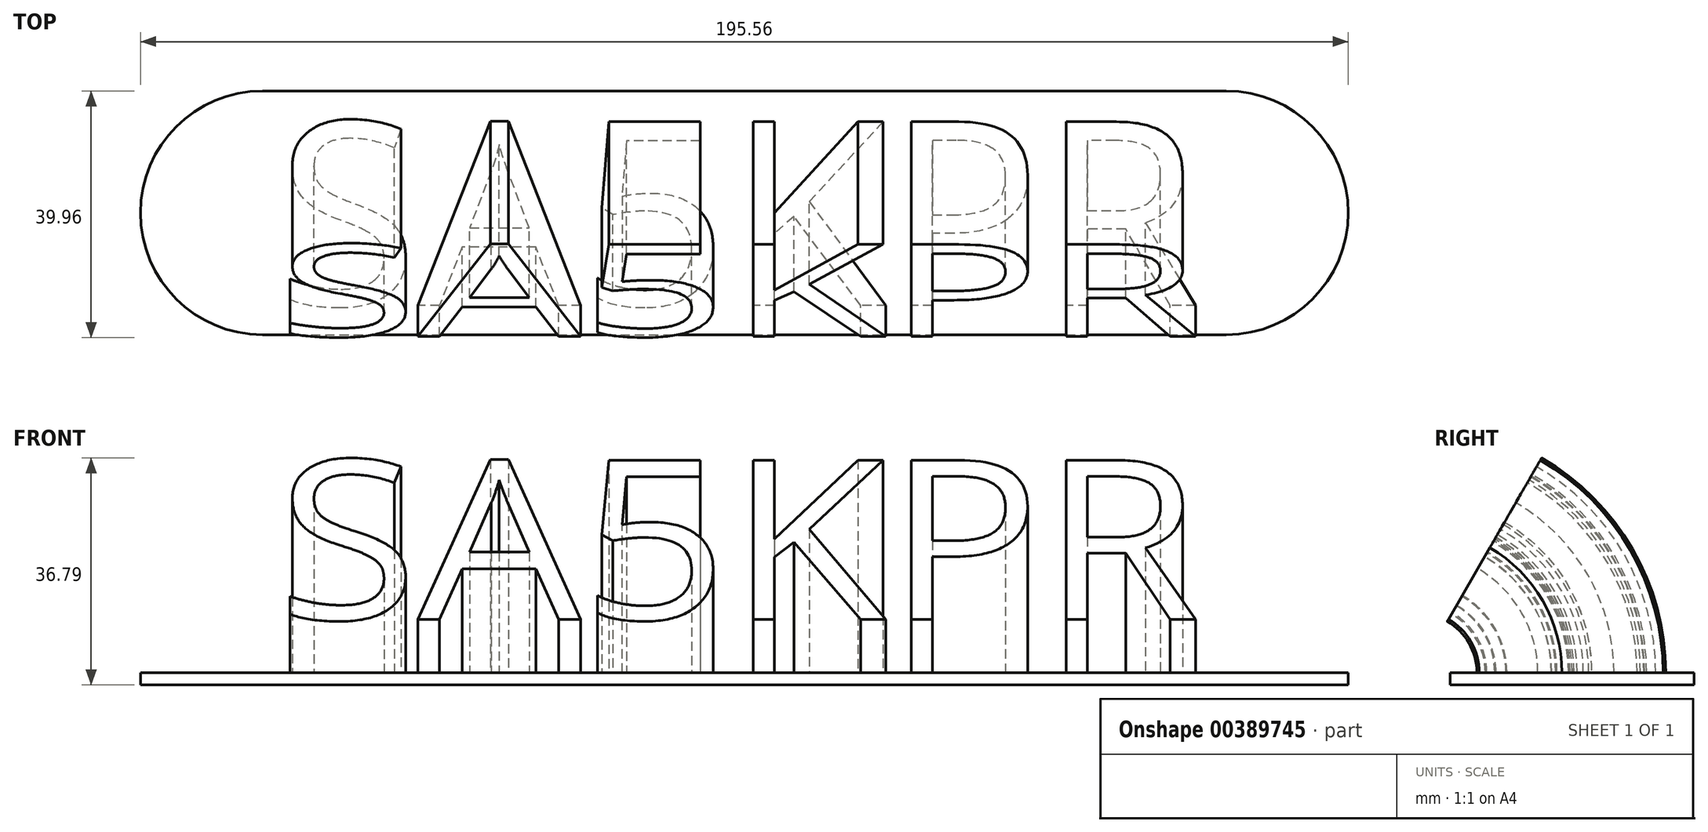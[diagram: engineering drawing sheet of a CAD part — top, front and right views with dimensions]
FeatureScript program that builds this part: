
annotation { "Feature Type Name" : "Feature", "Feature Type Description" : "" }
export const myFeature = defineFeature(function(context is Context, id is Id, definition is map)
    precondition{}
    {
        {
            var Q0;
            Q0=qCreatedBy(makeId("Top.planeOp"),FACE);
            var sketch = newSketch(context, id + "F0", { "sketchPlane" : qUnion([Q0])});
            skText(sketch, "E0", { "text": "SA5KPR", "fontName": "OpenSans-Regular.ttf"});
            skLineSegment(sketch, "E1", {"start": v(-75.73, -25) * mm, "end": v(75.73, -25) * mm});
            const initialGuessF0  = {"E0": [-0.07573, -0.015, 1, 0, 0.03]};
            skSetInitialGuess(sketch, initialGuessF0);
            skSolve(sketch);
        }
        {
            var Q0;
            Q0 = qSketchRegion(id + "F0", true);
            var Q1;
            Q1=sQuery(id+"F0.wireOp",EDGE,"E1");
            revolve(context, id + "F1", {"entities" : qUnion([Q0]), "axis" : qUnion([Q1]), "revolveType" : RevolveType.ONE_DIRECTION, "angle" : 60 * degree});
        }
        {
            var Q0;
            Q0=qCreatedBy(makeId("Top.planeOp"),FACE);
            var sketch = newSketch(context, id + "F2", { "sketchPlane" : qUnion([Q0])});
            skLineSegment(sketch, "E2", {"start": v(-78.03, -19.75) * mm, "end": v(78.03, -19.75) * mm});
            skLineSegment(sketch, "E3", {"start": v(78.03, 19.75) * mm, "end": v(-78.03, 19.75) * mm});
            skArc(sketch, "E4", {"start": v(78.03, 19.75) * mm, "mid": v(97.78, 0) * mm, "end": v(78.03, -19.75) * mm});
            skArc(sketch, "E5", {"start": v(-78.03, 19.75) * mm, "mid": v(-97.78, 0) * mm, "end": v(-78.03, -19.75) * mm});
            skSolve(sketch);
        }
        {
            var Q0;
            Q0 = qSketchRegion(id + "F2", true);
            extrude(context, id + "F3", {"entities" : qUnion([Q0]), "operationType" : NewBodyOperationType.ADD, "oppositeDirection" : true, "depth" : 2 * mm, "offsetDistance" : 25 * mm});
        }
    });
